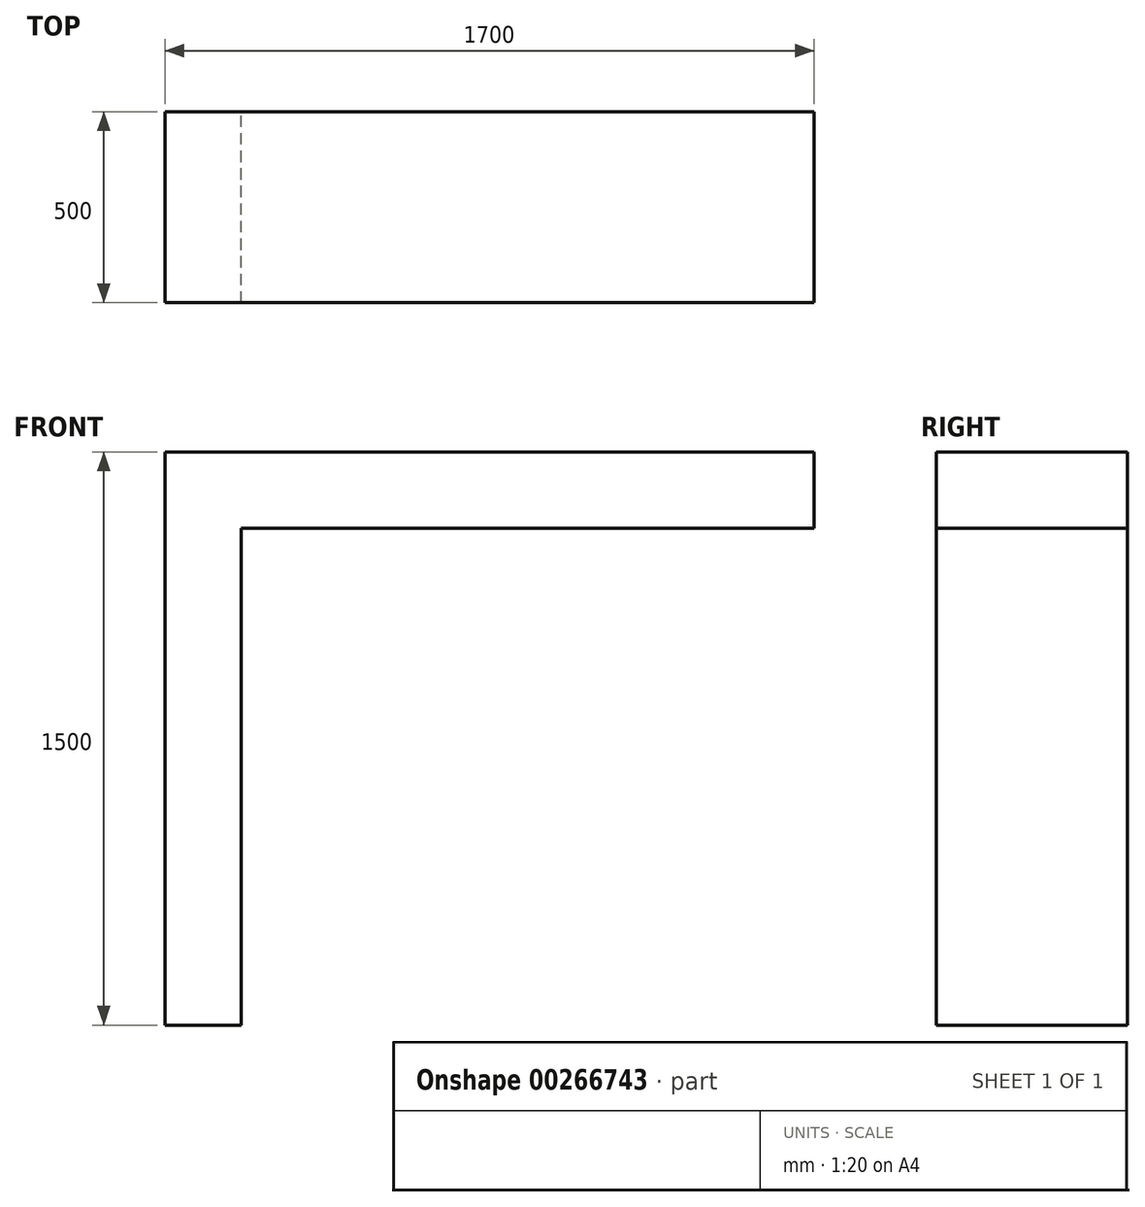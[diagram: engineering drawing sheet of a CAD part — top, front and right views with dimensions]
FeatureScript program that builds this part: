
annotation { "Feature Type Name" : "Feature", "Feature Type Description" : "" }
export const myFeature = defineFeature(function(context is Context, id is Id, definition is map)
    precondition{}
    {
        {
            var Q0;
            Q0=qCreatedBy(makeId("Front.planeOp"),FACE);
            var sketch = newSketch(context, id + "F0", { "sketchPlane" : qUnion([Q0])});
            skLineSegment(sketch, "E0", {"start": v(0, 0) * mm, "end": v(-200, 0) * mm});
            skLineSegment(sketch, "E1", {"start": v(-200, 0) * mm, "end": v(-200, 1500) * mm});
            skLineSegment(sketch, "E2", {"start": v(-200, 1500) * mm, "end": v(1500, 1500) * mm});
            skLineSegment(sketch, "E3", {"start": v(1500, 1500) * mm, "end": v(1500, 1300) * mm});
            skLineSegment(sketch, "E4", {"start": v(1500, 1300) * mm, "end": v(0, 1300) * mm});
            skLineSegment(sketch, "E5", {"start": v(0, 1300) * mm, "end": v(0, 0) * mm});
            skSolve(sketch);
        }
        {
            var Q0;
            Q0=makeQuery(id+"F0.imprint","IMPRINT",FACE,{"disambiguationData":[TD([[makeQuery(id+"F0.imprint","IMPRINT",EDGE,{"derivedFrom":sQuery(id+"F0.wireOp",EDGE,"E0")}),-1.0]])]});
            extrude(context, id + "F1", {"entities" : qUnion([Q0]), "depth" : 500 * mm});
        }
    });
